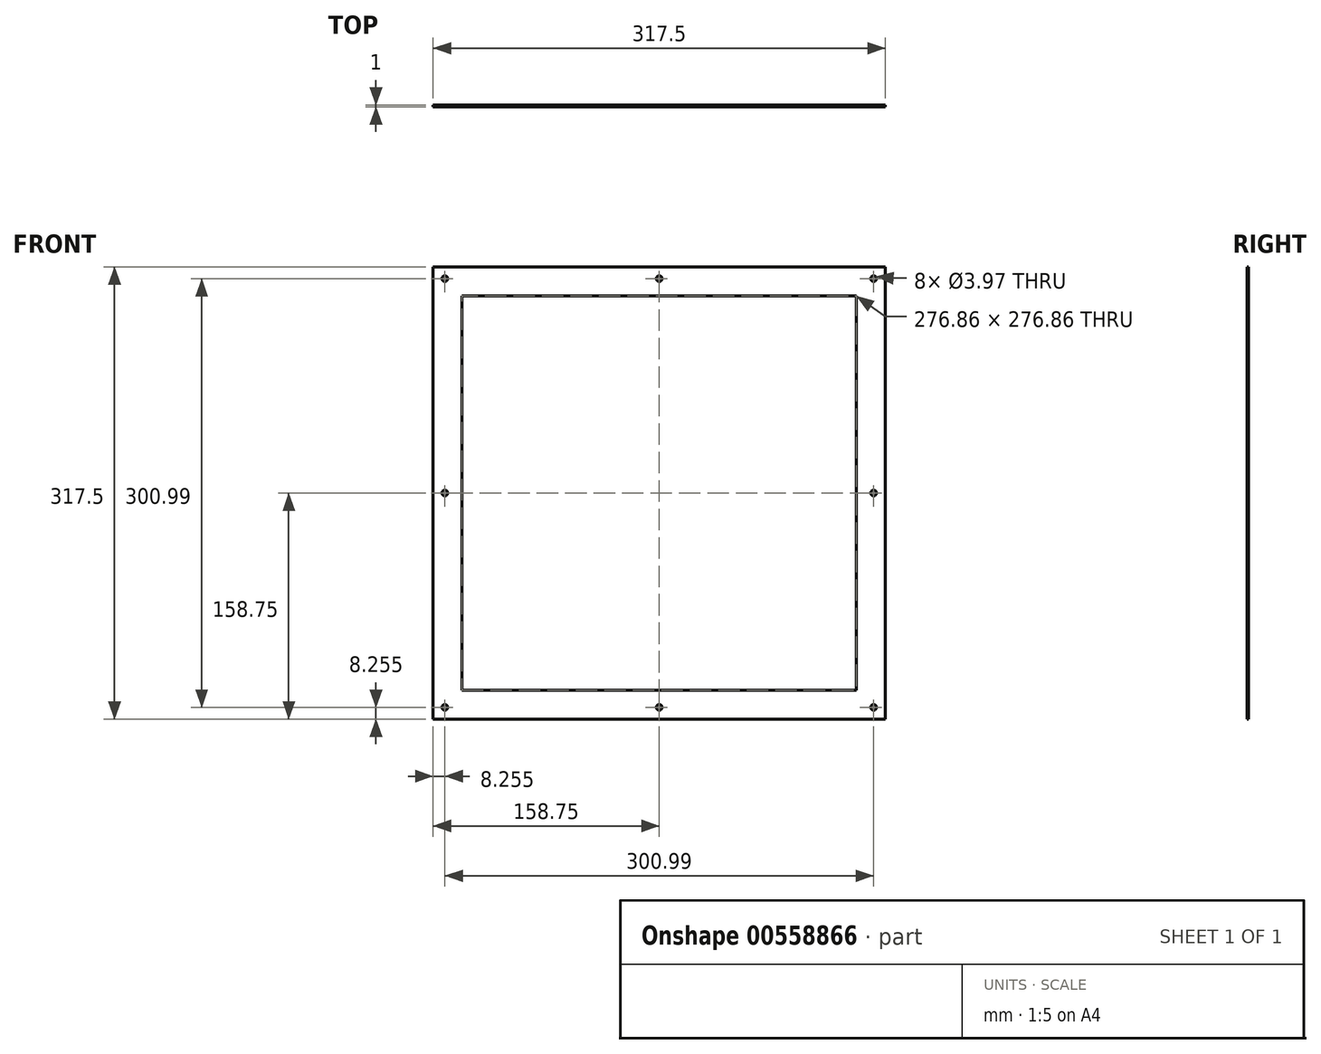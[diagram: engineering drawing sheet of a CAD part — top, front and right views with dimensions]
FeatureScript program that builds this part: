
annotation { "Feature Type Name" : "Feature", "Feature Type Description" : "" }
export const myFeature = defineFeature(function(context is Context, id is Id, definition is map)
    precondition{}
    {
        {
            var Q0;
            Q0=qCreatedBy(makeId("Front.planeOp"),FACE);
            var sketch = newSketch(context, id + "F0", { "sketchPlane" : qUnion([Q0])});
            skLineSegment(sketch, "E0.bottom", {"start": v(-158.75, 158.75) * mm, "end": v(158.75, 158.75) * mm});
            skLineSegment(sketch, "E0.top", {"start": v(-158.75, -158.75) * mm, "end": v(158.75, -158.75) * mm});
            skLineSegment(sketch, "E0.left", {"start": v(-158.75, 158.75) * mm, "end": v(-158.75, -158.75) * mm});
            skLineSegment(sketch, "E0.right", {"start": v(158.75, 158.75) * mm, "end": v(158.75, -158.75) * mm});
            skPoint(sketch, "E0.middle", {"position": v(0, 0) * mm});
            skCircle(sketch, "E1", {"center": v(-150.5, 150.5) * mm, "radius": 1.98 * mm});
            skCircle(sketch, "E2", {"center": v(0, 150.5) * mm, "radius": 1.98 * mm});
            skCircle(sketch, "E3", {"center": v(150.5, 150.5) * mm, "radius": 1.98 * mm});
            skLineSegment(sketch, "E4", {"start": v(-158.75, 0) * mm, "end": v(158.75, 0) * mm, "construction": true});
            skCircle(sketch, "E5.MirrorC", {"center": v(150.5, -150.5) * mm, "radius": 1.98 * mm});
            skCircle(sketch, "E6.MirrorC", {"center": v(-150.5, -150.5) * mm, "radius": 1.98 * mm});
            skCircle(sketch, "E7.MirrorC", {"center": v(0, -150.5) * mm, "radius": 1.98 * mm});
            skLineSegment(sketch, "E8", {"start": v(0, 158.75) * mm, "end": v(0, -158.75) * mm, "construction": true});
            skCircle(sketch, "E9", {"center": v(-150.5, 0) * mm, "radius": 1.98 * mm});
            skCircle(sketch, "E10.MirrorC", {"center": v(150.5, 0) * mm, "radius": 1.98 * mm});
            skLineSegment(sketch, "E11.bottom", {"start": v(138.43, 138.43) * mm, "end": v(-138.43, 138.43) * mm});
            skLineSegment(sketch, "E11.top", {"start": v(138.43, -138.43) * mm, "end": v(-138.43, -138.43) * mm});
            skLineSegment(sketch, "E11.left", {"start": v(138.43, 138.43) * mm, "end": v(138.43, -138.43) * mm});
            skLineSegment(sketch, "E11.right", {"start": v(-138.43, 138.43) * mm, "end": v(-138.43, -138.43) * mm});
            skSolve(sketch);
        }
        {
            var Q0;
            Q0=makeQuery(id+"F0.imprint","IMPRINT",FACE,{"disambiguationData":[TD([[makeQuery(id+"F0.imprint","IMPRINT",EDGE,{"derivedFrom":sQuery(id+"F0.wireOp",EDGE,"E0.bottom")}),-1.0]])]});
            extrude(context, id + "F1", {"entities" : qUnion([Q0]), "depth" : 1 * mm, "offsetDistance" : 25 * mm});
        }
    });
